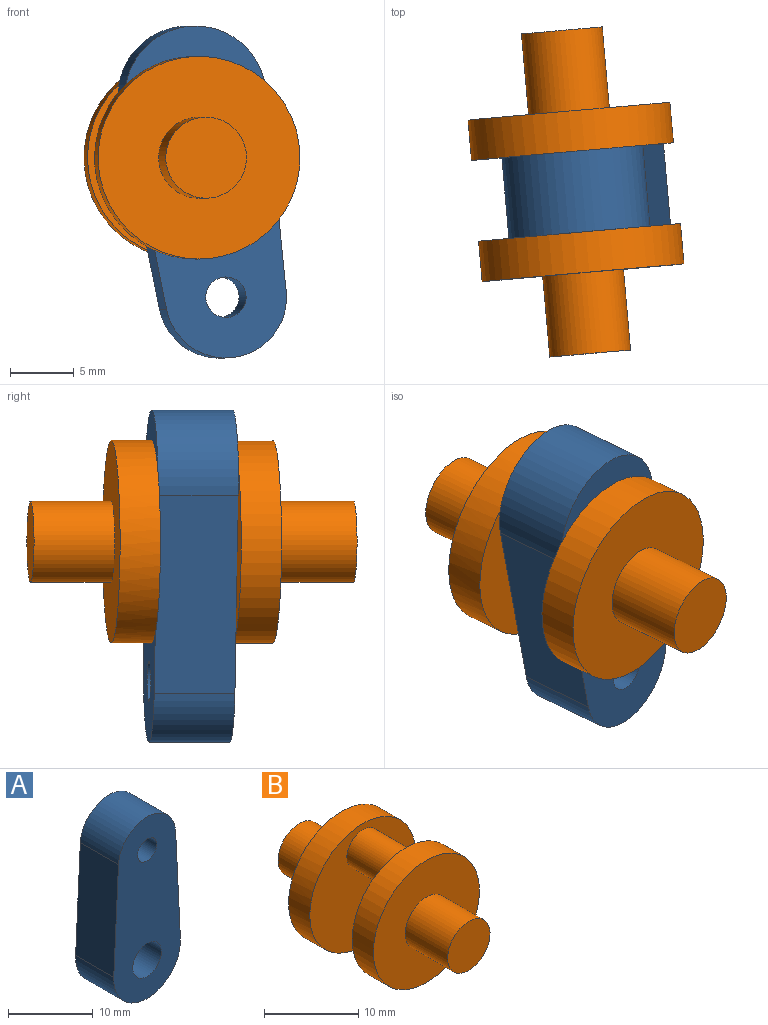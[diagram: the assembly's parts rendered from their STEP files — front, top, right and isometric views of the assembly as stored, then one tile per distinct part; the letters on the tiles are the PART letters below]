
ASSEMBLY  parts=2 mates=1
PART A: 8 faces, bbox 11.1x6.4x26.2 mm
  f0: plane 15.84x6.35mm, normal (-1,0,0.05), area 100.7mm2, adj f1,f4,f6,f7
  f1: cylinder r=5.56mm len=11.11mm, axis (0,1,0), area 114.4mm2, adj f0,f2,f6,f7
  f2: plane 15.84x6.35mm, normal (1,0,0.05), area 100.7mm2, adj f1,f4,f6,f7
  f3: cylinder r=2.38mm len=6.35mm, axis (0,1,0), area 95mm2, adj f6,f7
  f4: cylinder r=4.76mm len=9.51mm, axis (0,1,0), area 92mm2, adj f0,f2,f6,f7
  f5: cylinder r=1.59mm len=6.35mm, axis (0,1,0), area 63.3mm2, adj f6,f7
  f6: plane 26.19x11.11mm, normal (0,-1,0), area 222.4mm2, adj f0,f1,f2,f3,f4,f5
  f7: plane 26.19x11.11mm, normal (0,1,0), area 222.4mm2, adj f0,f1,f2,f3,f4,f5
PART B: 11 faces, bbox 15.9x25.4x15.9 mm
  f0: cylinder r=7.94mm len=15.88mm, axis (0,1,0), area 158.3mm2, adj f2,f8
  f1: cylinder r=7.94mm len=15.88mm, axis (0,1,0), area 158.3mm2, adj f3,f5
  f2: plane 15.88x15.88mm, normal (0,-1,0), area 180.1mm2, adj f0,f4
  f3: plane 15.88x15.88mm, normal (0,1,0), area 180.1mm2, adj f1,f4
  f4: cylinder r=2.38mm len=6.35mm, axis (0,-1,0), area 95mm2, adj f2,f3
  f5: plane 15.88x15.88mm, normal (0,-1,0), area 166.3mm2, adj f1,f6
  f6: cylinder r=3.17mm len=6.35mm, axis (0,-1,0), area 126.7mm2, adj f5,f7
  f7: plane 6.35x6.35mm, normal (0,-1,0), area 31.7mm2, adj f6
  f8: plane 15.88x15.88mm, normal (0,1,0), area 166.3mm2, adj f0,f9
  f9: cylinder r=3.17mm len=6.35mm, axis (0,1,0), area 126.7mm2, adj f8,f10
  f10: plane 6.35x6.35mm, normal (0,1,0), area 31.7mm2, adj f9
PLACE A rot(axis=(-0.04,1,0),171.3deg) t=(-1.96,-0.93,3.02)mm
PLACE B rot(axis=(0,0,1),5deg) t=(-1.25,-0.87,-6.45)mm fixed
MATE revolute B.f4 <-> A.f3  axis (0.09,-1,0) through (-1.25,-0.87,-1.69)mm
